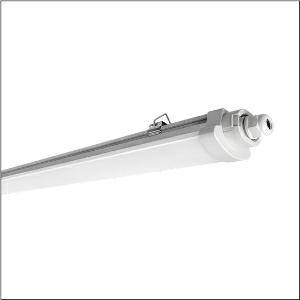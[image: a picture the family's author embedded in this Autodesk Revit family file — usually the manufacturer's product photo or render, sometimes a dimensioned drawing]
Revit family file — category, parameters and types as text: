
# Revit family: monsun_r__41_51fk20mk440a_a1bd
name_source: partatom
category: Lighting Fixtures
units: mm (PartAtom-declared; Revit-internal decimal feet)

## family parameters
Cut with Voids When Loaded = No
Host = Face
Light Source = No
Part Type = Normal
Room Calculation Point = No
Round Connector Dimension = Use Diameter
Shared = No

## types (1)
- --- (1 x LED, 4000 lm, 30 W, 4000K)
    Apparent Load = 30 VA
    CIE Flux Codes = 44 74 92 92 100
    Color Rendering = 80
    Color Temperature = 4000K
    Default Elevation = 1800 mm
    Description = Monsun® 41, damp-proof luminaire, primary optical cover: diffuser, of PC, frosted, light emission: direct distribution, primary light characteristic: symmetric, installation type: surface-mounted, suspended mounting, LED, rated luminous flux: 4.000lm, luminous efficacy: 130lm/W, light colour: 840, colour temperature: 4000K, control gear: ECG Multilumen, with terminal, 3-pole, mains connection: 220..240V, AC, 50/60Hz, rated input power: 30W, housing, luminaire housing, of PC, grey, length: 1.200mm, width: 79mm, height: 52mm, end cap, of PC, grey, ceiling mounting element, of stainless steel (V2A), protection rating (complete): IP65, insulation class (complete): insulation class II (safety insulation), certification: CE, UKCA, protection symbol: D, impact resistance: IK08, permissible operating ambient temperature: -20..+35°C, corresponds to IFS (International Featured Standards) requirements for safety and quality in the food industry, contact your sales advisor before using the luminaires in applications with unclear chemical exposure, large temperature fluctuations or condensation-forming humidity, packaging unit: 1 piece
    Height = 54 mm
    Lamp = 1 x LED
    Lamp Light Flux = 4000 lm
    Lamp Power = 30 W
    Lamp count = 1
    Length = 1200 mm
    Luminous efficacy = 133 lm/W
    Manufacturer = Siteco
    ModVariant = No
    Model = 51FK20MK440A
    Mounting Place = Ceiling
    Mounting Type = Surface mounted
    Number of Poles = 1
    OnlyDefault = Yes
    Power Factor = 1
    Product Name = Monsun® 41
    Product group = damp-proof luminaire
    ProductGroupID = 301
    Protection Class = Protection class II
    Protection Degree = IP 65
    RLX_Detail_Level = 1
    RLX_Emergency_Light_Flux = 0 lm
    RLX_Emergency_Type = 0
    RLX_Emergency_Type_DB = No
    RlxData = <blob elided: 31833 chars, md5=d442aa40>
    Socket = socket
    Standby Power = 0 W
    System Light Flux = 4000 lm
    System Power = 30 W
    Type Comments = factory setting: luminous flux: 100 % | (HIGH)
    Type Image = l_1007037.jpg
    URL = http://relux.com
    VarID = @adj_125709
    Voltage = 0 V
    Weight = 0.00 kg
    Width = 79 mm

## geometry (parser evidence)
native form markers: Blend x4, Sweep x12
no freeform markers — native parametric forms only
